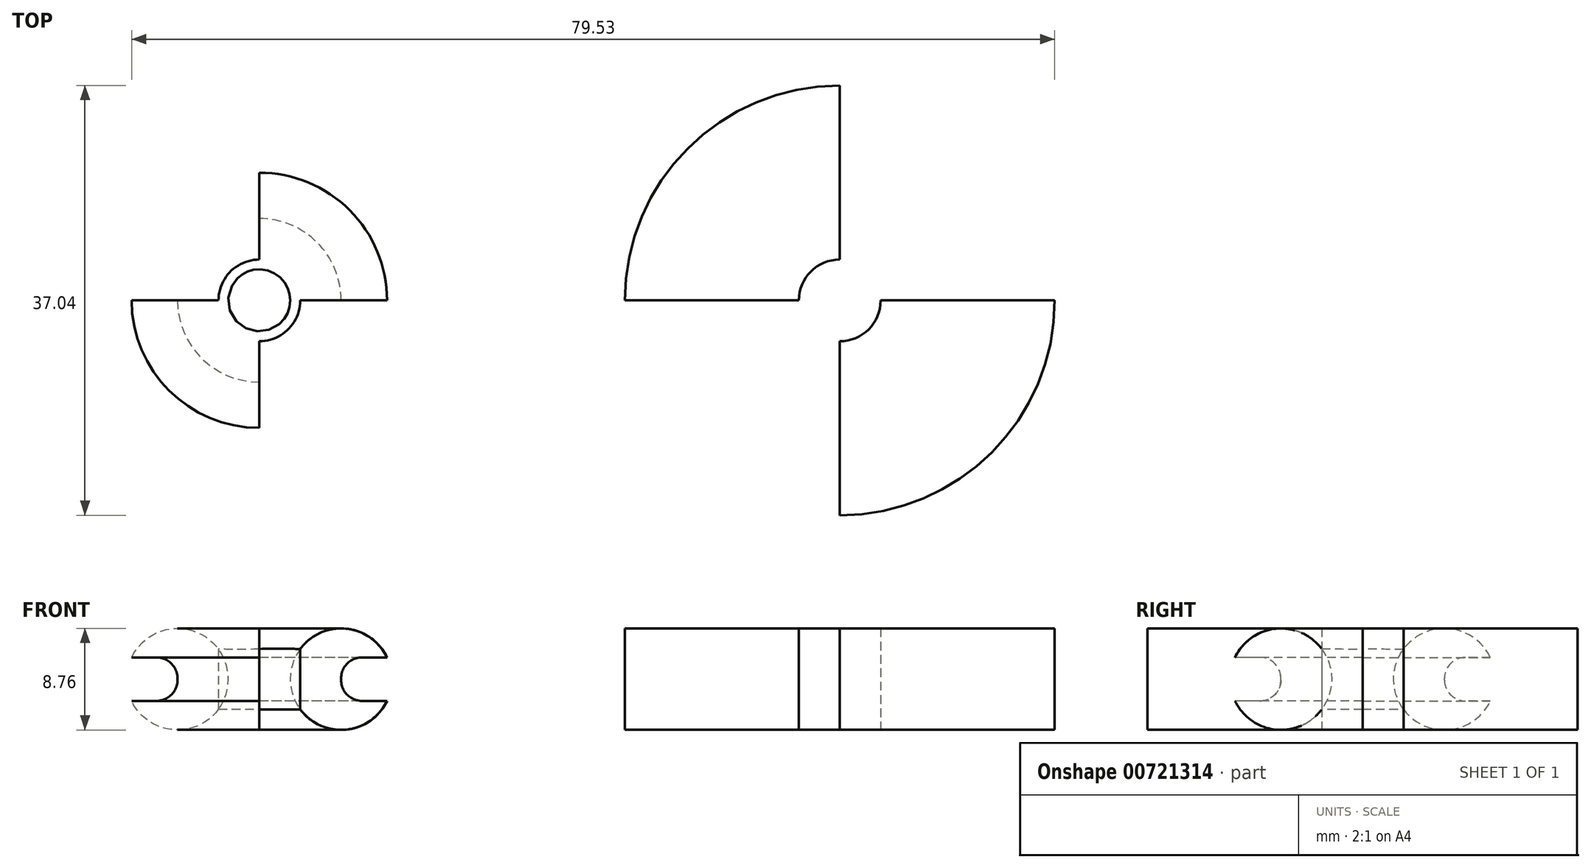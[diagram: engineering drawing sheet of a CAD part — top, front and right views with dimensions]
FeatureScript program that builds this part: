
annotation { "Feature Type Name" : "Feature", "Feature Type Description" : "" }
export const myFeature = defineFeature(function(context is Context, id is Id, definition is map)
    precondition{}
    {
        {
            var Q0;
            Q0=qCreatedBy(makeId("Front.planeOp"),FACE);
            var sketch = newSketch(context, id + "F0", { "sketchPlane" : qUnion([Q0])});
            skLineSegment(sketch, "E0", {"start": v(0, 6.53) * mm, "end": v(0, 4.38) * mm, "construction": true});
            skLineSegment(sketch, "E1.0", {"start": v(3.95, 1.87) * mm, "end": v(1.8, 1.87) * mm});
            skLineSegment(sketch, "E2.0", {"start": v(3.95, -1.88) * mm, "end": v(1.8, -1.88) * mm});
            skLineSegment(sketch, "E3", {"start": v(0, 0.07) * mm, "end": v(0, -0.08) * mm});
            skLineSegment(sketch, "E4", {"start": v(-3.95, 1.87) * mm, "end": v(-10.95, 1.87) * mm, "construction": true});
            skArc(sketch, "E5", {"start": v(3.95, 1.88) * mm, "mid": v(-4.38, 0) * mm, "end": v(3.95, -1.88) * mm});
            skLineSegment(sketch, "E6.trimOffspring", {"start": v(-4.38, 0) * mm, "end": v(-11.15, 0) * mm, "construction": true});
            skLineSegment(sketch, "E7.trimOffspring", {"start": v(-3.95, -1.88) * mm, "end": v(-10.82, -1.88) * mm, "construction": true});
            skLineSegment(sketch, "E8.0", {"start": v(-7.05, 1.87) * mm, "end": v(-7.05, -1.88) * mm, "construction": true});
            skPoint(sketch, "E9.orphan", {"position": v(-7.74, 1.87) * mm});
            skPoint(sketch, "E10.orphan", {"position": v(-7.74, -1.88) * mm});
            skPoint(sketch, "E11.orphan", {"position": v(-7.74, 0) * mm});
            skPoint(sketch, "E12.visualSharp", {"position": v(0, 1.87) * mm});
            skArc(sketch, "E12.filletArc", {"start": v(1.8, 1.87) * mm, "mid": v(0.53, 1.35) * mm, "end": v(0, 0.07) * mm});
            skPoint(sketch, "E13.visualSharp", {"position": v(0, -1.88) * mm});
            skArc(sketch, "E13.filletArc", {"start": v(0, -0.08) * mm, "mid": v(0.53, -1.35) * mm, "end": v(1.8, -1.88) * mm});
            skSolve(sketch);
        }
        {
            var Q0;
            Q0=makeQuery(id+"F0.imprint","IMPRINT",FACE,{"disambiguationData":[TD([[makeQuery(id+"F0.imprint","IMPRINT",EDGE,{"derivedFrom":sQuery(id+"F0.wireOp",EDGE,"E1.0")}),-1.0]])]});
            var Q1;
            Q1=sQuery(id+"F0.wireOp",EDGE,"E8.0");
            revolve(context, id + "F1", {"surfaceOperationType" : NewSurfaceOperationType.NEW, "entities" : qUnion([Q0]), "axis" : qUnion([Q1]), "revolveType" : RevolveType.FULL});
        }
        {
            var Q0;
            Q0=qCreatedBy(makeId("Top.planeOp"),FACE);
            var sketch = newSketch(context, id + "F2", { "sketchPlane" : qUnion([Q0])});
            skLineSegment(sketch, "E14", {"start": v(41.74, 19.1) * mm, "end": v(41.74, 0) * mm, "construction": true});
            skLineSegment(sketch, "E15", {"start": v(24.18, 0) * mm, "end": v(41.74, 0) * mm, "construction": true});
            skLineSegment(sketch, "E16", {"start": v(41.74, 0) * mm, "end": v(41.74, -23.58) * mm, "construction": true});
            skLineSegment(sketch, "E17", {"start": v(41.74, 0) * mm, "end": v(57.75, 0) * mm, "construction": true});
            skArc(sketch, "E18", {"start": v(41.74, 3.52) * mm, "mid": v(39.25, 2.5) * mm, "end": v(38.22, 0) * mm});
            skArc(sketch, "E19.trimOffspring", {"start": v(41.74, -3.52) * mm, "mid": v(44.23, -2.5) * mm, "end": v(45.27, 0) * mm});
            skLineSegment(sketch, "E20", {"start": v(36.24, 0) * mm, "end": v(38.22, 0) * mm});
            skLineSegment(sketch, "E21", {"start": v(41.74, 5.5) * mm, "end": v(41.74, 3.52) * mm});
            skLineSegment(sketch, "E22", {"start": v(45.27, 0) * mm, "end": v(47.24, 0) * mm});
            skLineSegment(sketch, "E23", {"start": v(41.74, -3.52) * mm, "end": v(41.74, -5.5) * mm});
            skArc(sketch, "E24.0", {"start": v(41.74, 18.52) * mm, "mid": v(28.64, 13.1) * mm, "end": v(23.22, 0) * mm});
            skArc(sketch, "E25.0", {"start": v(41.74, -18.52) * mm, "mid": v(54.84, -13.1) * mm, "end": v(60.27, 0) * mm});
            skLineSegment(sketch, "E26", {"start": v(23.22, 0) * mm, "end": v(38.22, 0) * mm});
            skLineSegment(sketch, "E27", {"start": v(41.74, 3.52) * mm, "end": v(41.74, 18.52) * mm});
            skLineSegment(sketch, "E28", {"start": v(60.27, 0) * mm, "end": v(45.27, 0) * mm});
            skLineSegment(sketch, "E29", {"start": v(41.74, -3.52) * mm, "end": v(41.74, -18.52) * mm});
            skSolve(sketch);
        }
        {
            var Q0;
            Q0=makeQuery(id+"F1.opRevolve","SWEPT_BODY",BODY,{"disambiguationData":[OSD([sQuery(id+"F0.wireOp",EDGE,"E1.0"),sQuery(id+"F0.wireOp",EDGE,"E2.0"),sQuery(id+"F0.wireOp",EDGE,"E3"),sQuery(id+"F0.wireOp",EDGE,"E5"),sQuery(id+"F0.wireOp",EDGE,"E12.filletArc"),sQuery(id+"F0.wireOp",EDGE,"E13.filletArc")])]});
            transform(context, id + "F3", {"entities" : qUnion([Q0]), "transformType" : TransformType.TRANSLATION_3D, "dx" : 7 * mm, "dy" : -0.2 * mm, "dz" : 0 * mm, "makeCopy" : false});
        }
        {
            var Q0;
            Q0=makeQuery(id+"F1.opRevolve","SWEPT_BODY",BODY,{"disambiguationData":[OSD([sQuery(id+"F0.wireOp",EDGE,"E1.0"),sQuery(id+"F0.wireOp",EDGE,"E2.0"),sQuery(id+"F0.wireOp",EDGE,"E3"),sQuery(id+"F0.wireOp",EDGE,"E5"),sQuery(id+"F0.wireOp",EDGE,"E12.filletArc"),sQuery(id+"F0.wireOp",EDGE,"E13.filletArc")])]});
            transform(context, id + "F4", {"entities" : qUnion([Q0]), "transformType" : TransformType.TRANSLATION_3D, "dx" : 0.04 * mm, "dy" : 0.2 * mm, "dz" : 0 * mm, "makeCopy" : false});
        }
        {
            var Q0;
            Q0 = qSketchRegion(id + "F2", true);
            extrude(context, id + "F5", {"entities" : qUnion([Q0]), "depth" : 8.75 * mm, "offsetDistance" : 25 * mm});
        }
        {
            var Q0;
            Q0=makeQuery(id+"F5.opExtrude","SWEPT_BODY",BODY,{"disambiguationData":[OSD([sQuery(id+"F2.wireOp",EDGE,"E19.trimOffspring"),sQuery(id+"F2.wireOp",EDGE,"E25.0"),sQuery(id+"F2.wireOp",EDGE,"E28"),sQuery(id+"F2.wireOp",EDGE,"E29")])]});
            var Q1;
            Q1=makeQuery(id+"F5.opExtrude","SWEPT_BODY",BODY,{"disambiguationData":[OSD([sQuery(id+"F2.wireOp",EDGE,"E18"),sQuery(id+"F2.wireOp",EDGE,"E24.0"),sQuery(id+"F2.wireOp",EDGE,"E26"),sQuery(id+"F2.wireOp",EDGE,"E27")])]});
            transform(context, id + "F6", {"entities" : qUnion([Q0, Q1]), "transformType" : TransformType.TRANSLATION_3D, "dx" : -41.74 * mm, "dy" : -10E-4 * mm, "dz" : 0 * mm, "makeCopy" : false});
        }
        {
            var Q0;
            Q0=makeQuery(id+"F5.opExtrude","SWEPT_BODY",BODY,{"disambiguationData":[OSD([sQuery(id+"F2.wireOp",EDGE,"E19.trimOffspring"),sQuery(id+"F2.wireOp",EDGE,"E25.0"),sQuery(id+"F2.wireOp",EDGE,"E28"),sQuery(id+"F2.wireOp",EDGE,"E29")])]});
            var Q1;
            Q1=makeQuery(id+"F5.opExtrude","SWEPT_BODY",BODY,{"disambiguationData":[OSD([sQuery(id+"F2.wireOp",EDGE,"E18"),sQuery(id+"F2.wireOp",EDGE,"E24.0"),sQuery(id+"F2.wireOp",EDGE,"E26"),sQuery(id+"F2.wireOp",EDGE,"E27")])]});
            transform(context, id + "F7", {"entities" : qUnion([Q0, Q1]), "transformType" : TransformType.TRANSLATION_3D, "dx" : 0 * mm, "dy" : 0 * mm, "dz" : -4.38 * mm, "makeCopy" : false});
        }
        {
            var Q0;
            Q0=makeQuery(id+"F5.opExtrude","SWEPT_BODY",BODY,{"disambiguationData":[OSD([sQuery(id+"F2.wireOp",EDGE,"E18"),sQuery(id+"F2.wireOp",EDGE,"E24.0"),sQuery(id+"F2.wireOp",EDGE,"E26"),sQuery(id+"F2.wireOp",EDGE,"E27")])]});
            var Q1;
            Q1=makeQuery(id+"F5.opExtrude","SWEPT_BODY",BODY,{"disambiguationData":[OSD([sQuery(id+"F2.wireOp",EDGE,"E19.trimOffspring"),sQuery(id+"F2.wireOp",EDGE,"E25.0"),sQuery(id+"F2.wireOp",EDGE,"E28"),sQuery(id+"F2.wireOp",EDGE,"E29")])]});
            var Q2;
            Q2=makeQuery(id+"F1.opRevolve","SWEPT_BODY",BODY,{"disambiguationData":[OSD([sQuery(id+"F0.wireOp",EDGE,"E1.0"),sQuery(id+"F0.wireOp",EDGE,"E2.0"),sQuery(id+"F0.wireOp",EDGE,"E3"),sQuery(id+"F0.wireOp",EDGE,"E5"),sQuery(id+"F0.wireOp",EDGE,"E12.filletArc"),sQuery(id+"F0.wireOp",EDGE,"E13.filletArc")])]});
            booleanBodies(context, id + "F8", {"operationType" : BooleanOperationType.SUBTRACTION, "tools" : qUnion([Q0, Q1]), "targets" : qUnion([Q2]), "keepTools" : true});
        }
        {
            var Q0;
            Q0=makeQuery(id+"F5.opExtrude","SWEPT_BODY",BODY,{"disambiguationData":[OSD([sQuery(id+"F2.wireOp",EDGE,"E19.trimOffspring"),sQuery(id+"F2.wireOp",EDGE,"E25.0"),sQuery(id+"F2.wireOp",EDGE,"E28"),sQuery(id+"F2.wireOp",EDGE,"E29")])]});
            var Q1;
            Q1=makeQuery(id+"F5.opExtrude","SWEPT_BODY",BODY,{"disambiguationData":[OSD([sQuery(id+"F2.wireOp",EDGE,"E18"),sQuery(id+"F2.wireOp",EDGE,"E24.0"),sQuery(id+"F2.wireOp",EDGE,"E26"),sQuery(id+"F2.wireOp",EDGE,"E27")])]});
            transform(context, id + "F9", {"entities" : qUnion([Q0, Q1]), "transformType" : TransformType.TRANSLATION_3D, "dx" : 50 * mm, "dy" : 0 * mm, "dz" : 0 * mm, "makeCopy" : false});
        }
    });
